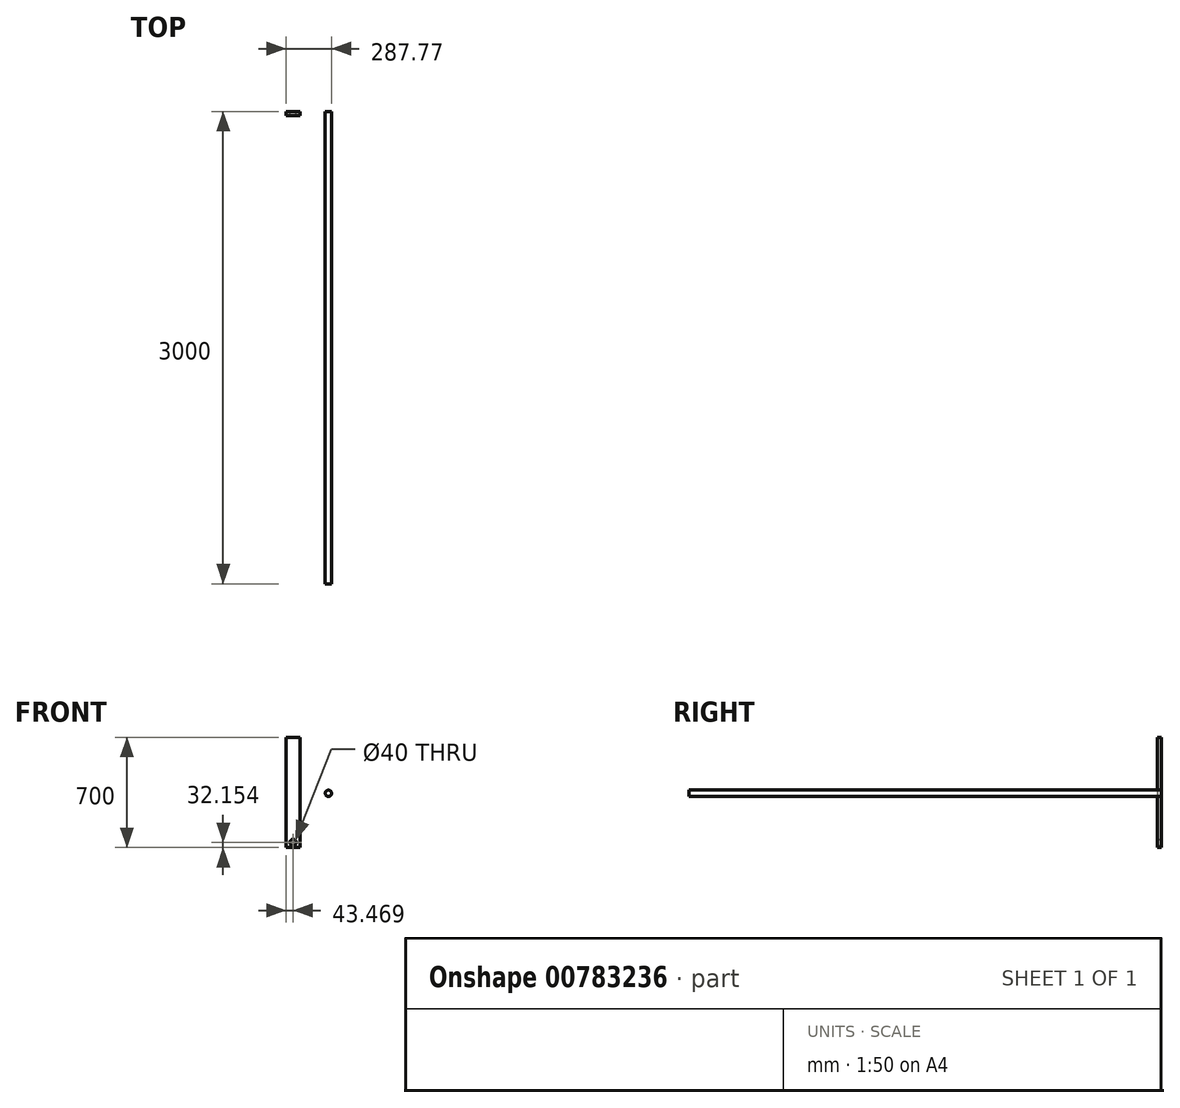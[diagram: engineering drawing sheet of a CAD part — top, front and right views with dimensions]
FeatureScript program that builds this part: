
annotation { "Feature Type Name" : "Feature", "Feature Type Description" : "" }
export const myFeature = defineFeature(function(context is Context, id is Id, definition is map)
    precondition{}
    {
        {
            var Q0;
            Q0=qCreatedBy(makeId("Front.planeOp"),FACE);
            var sketch = newSketch(context, id + "F0", { "sketchPlane" : qUnion([Q0])});
            skLineSegment(sketch, "E0.bottom", {"start": v(64.13, 137.17) * mm, "end": v(-23.46, 137.17) * mm});
            skLineSegment(sketch, "E0.top", {"start": v(64.13, -562.83) * mm, "end": v(-23.46, -562.83) * mm});
            skLineSegment(sketch, "E0.left", {"start": v(64.13, 137.17) * mm, "end": v(64.13, -562.83) * mm});
            skLineSegment(sketch, "E0.right", {"start": v(-23.46, 137.17) * mm, "end": v(-23.46, -562.83) * mm});
            skPoint(sketch, "E0.middle", {"position": v(20.34, -212.83) * mm});
            skCircle(sketch, "E1", {"center": v(20, -530.68) * mm, "radius": 20 * mm});
            skSolve(sketch);
        }
        {
            var Q0;
            Q0=makeQuery(id+"F0.imprint","IMPRINT",FACE,{"disambiguationData":[TD([[makeQuery(id+"F0.imprint","IMPRINT",EDGE,{"derivedFrom":sQuery(id+"F0.wireOp",EDGE,"E0.bottom")}),1.0]])]});
            extrude(context, id + "F1", {"entities" : qUnion([Q0]), "depth" : 25 * mm, "offsetDistance" : 25 * mm});
        }
        {
            var Q0;
            Q0=qCreatedBy(makeId("Front.planeOp"),FACE);
            var sketch = newSketch(context, id + "F2", { "sketchPlane" : qUnion([Q0])});
            skCircle(sketch, "E2", {"center": v(244.31, -218.58) * mm, "radius": 20 * mm});
            skSolve(sketch);
        }
        {
            var Q0;
            Q0 = qSketchRegion(id + "F2", true);
            extrude(context, id + "F3", {"entities" : qUnion([Q0]), "depth" : 3000 * mm, "offsetDistance" : 25 * mm});
        }
    });
